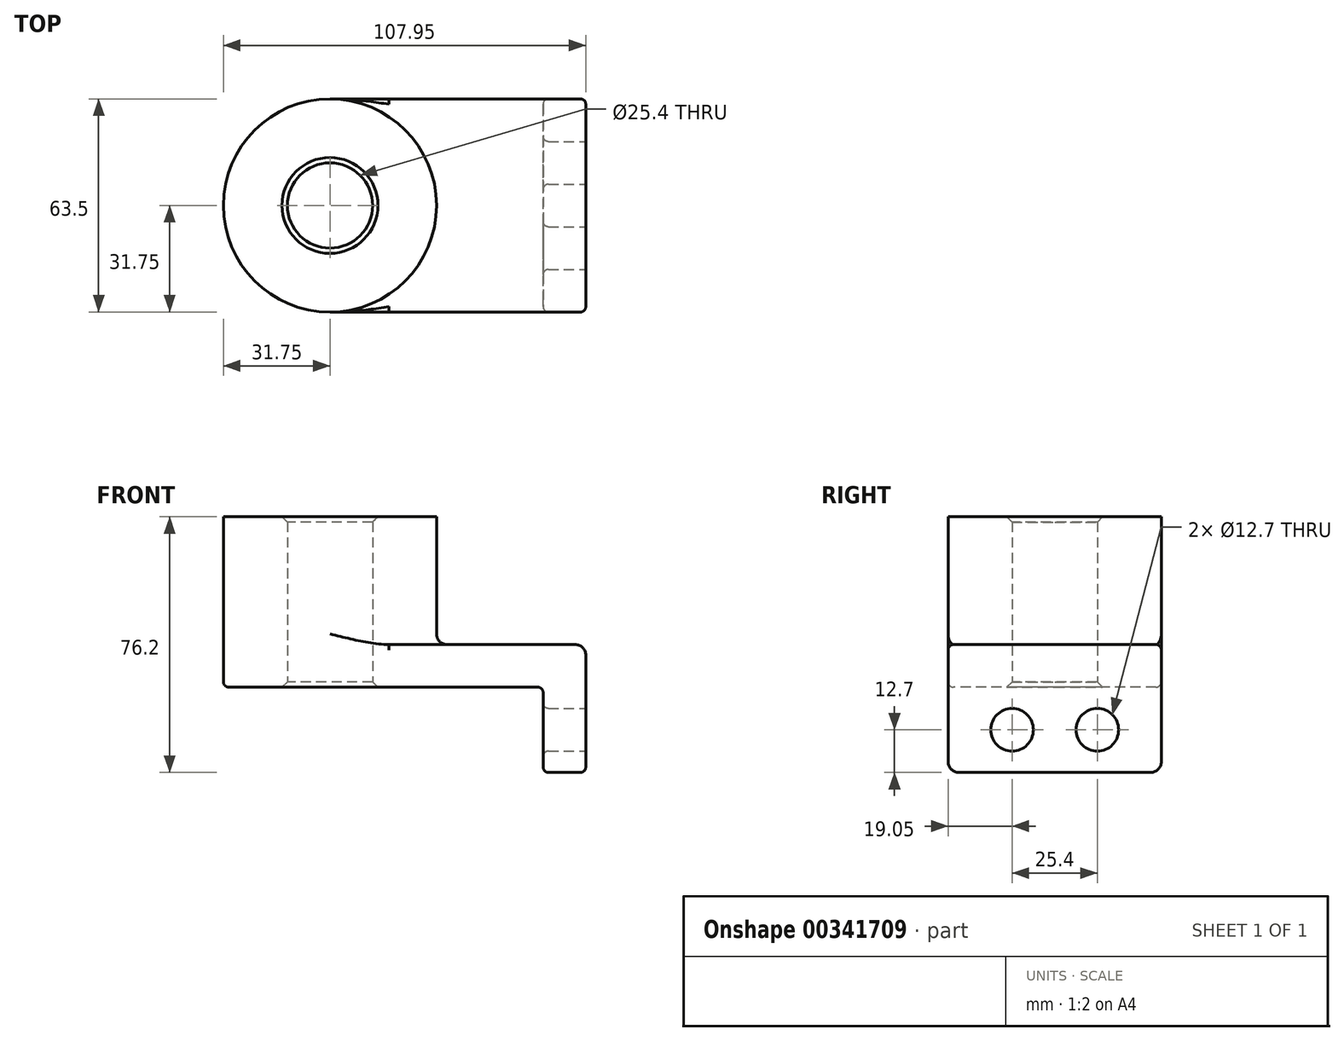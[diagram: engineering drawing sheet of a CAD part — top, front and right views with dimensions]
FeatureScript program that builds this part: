
annotation { "Feature Type Name" : "Feature", "Feature Type Description" : "" }
export const myFeature = defineFeature(function(context is Context, id is Id, definition is map)
    precondition{}
    {
        {
            var Q0;
            Q0=qCreatedBy(makeId("Top.planeOp"),FACE);
            var sketch = newSketch(context, id + "F0", { "sketchPlane" : qUnion([Q0])});
            skLineSegment(sketch, "E0.bottom", {"start": v(-38.1, 31.75) * mm, "end": v(38.1, 31.75) * mm});
            skLineSegment(sketch, "E0.top", {"start": v(-38.1, -31.75) * mm, "end": v(38.1, -31.75) * mm});
            skLineSegment(sketch, "E0.left", {"start": v(-38.1, 31.75) * mm, "end": v(-38.1, -31.75) * mm});
            skLineSegment(sketch, "E0.right", {"start": v(38.1, 31.75) * mm, "end": v(38.1, -31.75) * mm});
            skPoint(sketch, "E0.middle", {"position": v(0, 0) * mm});
            skCircle(sketch, "E1", {"center": v(-38.1, 0) * mm, "radius": 31.75 * mm});
            skPoint(sketch, "E1.centerSnap0", {"position": v(-38.1, 0) * mm});
            skCircle(sketch, "E2", {"center": v(-38.1, 0) * mm, "radius": 12.7 * mm});
            skSolve(sketch);
        }
        {
            var Q0;
            {var subQ1=sQuery(id+"F0.wireOp",EDGE,"E0.left");var subQ3=sQuery(id+"F0.wireOp",EDGE,"E2");var subQ4=makeQuery(id+"F0.imprint","INTERSECT",VERTEX,{"disambiguationData":[OD(0.0)],"derivedFrom":[subQ1,subQ3]});Q0=makeQuery(id+"F0.imprint","IMPRINT",FACE,{"disambiguationData":[TD([[makeQuery(id+"F0.imprint","IMPRINT",EDGE,{"disambiguationData":[TD([[subQ4,-1.0]])],"derivedFrom":subQ3}),-1.0]])]});}
            var Q1;
            {var subQ1=sQuery(id+"F0.wireOp",EDGE,"E0.left");var subQ3=sQuery(id+"F0.wireOp",EDGE,"E2");var subQ4=makeQuery(id+"F0.imprint","INTERSECT",VERTEX,{"disambiguationData":[OD(0.0)],"derivedFrom":[subQ1,subQ3]});Q1=makeQuery(id+"F0.imprint","IMPRINT",FACE,{"disambiguationData":[TD([[makeQuery(id+"F0.imprint","IMPRINT",EDGE,{"disambiguationData":[TD([[subQ4,1.0]])],"derivedFrom":subQ3}),-1.0]])]});}
            var Q2;
            {var subQ0=sQuery(id+"F0.wireOp",EDGE,"E0.bottom");Q2=makeQuery(id+"F0.imprint","IMPRINT",FACE,{"disambiguationData":[TD([[makeQuery(id+"F0.imprint","IMPRINT",EDGE,{"derivedFrom":subQ0}),-1.0]])]});}
            extrude(context, id + "F1", {"entities" : qUnion([Q0, Q1, Q2]), "depth" : 12.7 * mm});
        }
        {
            var Q0;
            {var subQ1=sQuery(id+"F0.wireOp",EDGE,"E0.left");var subQ3=sQuery(id+"F0.wireOp",EDGE,"E2");var subQ4=makeQuery(id+"F0.imprint","INTERSECT",VERTEX,{"disambiguationData":[OD(0.0)],"derivedFrom":[subQ1,subQ3]});Q0=makeQuery(id+"F0.imprint","IMPRINT",FACE,{"disambiguationData":[TD([[makeQuery(id+"F0.imprint","IMPRINT",EDGE,{"disambiguationData":[TD([[subQ4,1.0]])],"derivedFrom":subQ3}),-1.0]])]});}
            var Q1;
            {var subQ1=sQuery(id+"F0.wireOp",EDGE,"E0.left");var subQ3=sQuery(id+"F0.wireOp",EDGE,"E2");var subQ4=makeQuery(id+"F0.imprint","INTERSECT",VERTEX,{"disambiguationData":[OD(0.0)],"derivedFrom":[subQ1,subQ3]});Q1=makeQuery(id+"F0.imprint","IMPRINT",FACE,{"disambiguationData":[TD([[makeQuery(id+"F0.imprint","IMPRINT",EDGE,{"disambiguationData":[TD([[subQ4,-1.0]])],"derivedFrom":subQ3}),-1.0]])]});}
            extrude(context, id + "F2", {"entities" : qUnion([Q0, Q1]), "operationType" : NewBodyOperationType.ADD, "depth" : 50.8 * mm});
        }
        {
            var Q0;
            Q0=makeQuery(id+"F1.opExtrude","SWEPT_FACE",FACE,{"disambiguationData":[OSD([sQuery(id+"F0.wireOp",EDGE,"E0.right")])]});
            var sketch = newSketch(context, id + "F3", { "sketchPlane" : qUnion([Q0])});
            skLineSegment(sketch, "E3.top", {"start": v(-31.75, -25.4) * mm, "end": v(0.46, -25.4) * mm});
            skLineSegment(sketch, "E3.left", {"start": v(-31.75, 12.7) * mm, "end": v(-31.75, -25.4) * mm});
            skCircle(sketch, "E4", {"center": v(-12.7, -12.7) * mm, "radius": 6.35 * mm});
            skLineSegment(sketch, "E5", {"start": v(0, 0) * mm, "end": v(0, -25.4) * mm});
            skPoint(sketch, "E5.endSnap0", {"position": v(0.46, -25.4) * mm});
            skCircle(sketch, "E6.MirrorC", {"center": v(12.7, -12.7) * mm, "radius": 6.35 * mm});
            skPoint(sketch, "E7.orphan", {"position": v(32.68, -25.4) * mm});
            skPoint(sketch, "E8.end.orphan", {"position": v(0.46, -26.49) * mm});
            skLineSegment(sketch, "E9", {"start": v(0, -25.4) * mm, "end": v(31.75, -25.4) * mm});
            skLineSegment(sketch, "E10", {"start": v(31.75, -25.4) * mm, "end": v(31.75, 0) * mm});
            skLineSegment(sketch, "E11", {"start": v(31.75, 0) * mm, "end": v(-31.75, 0) * mm});
            skSolve(sketch);
        }
        {
            var Q0;
            {var subQ2=sQuery(id+"F3.wireOp",EDGE,"E5");Q0=makeQuery(id+"F3.imprint","IMPRINT",FACE,{"disambiguationData":[TD([[makeQuery(id+"F3.imprint","IMPRINT",EDGE,{"derivedFrom":subQ2}),1.0]])]});}
            var Q1;
            {var subQ4=sQuery(id+"F3.wireOp",EDGE,"E3.top");Q1=makeQuery(id+"F3.imprint","IMPRINT",FACE,{"disambiguationData":[TD([[makeQuery(id+"F3.imprint","IMPRINT",EDGE,{"derivedFrom":subQ4}),1.0]])]});}
            extrude(context, id + "F4", {"entities" : qUnion([Q0, Q1]), "operationType" : NewBodyOperationType.ADD, "depth" : -12.7 * mm});
        }
        {
            var Q0;
            Q0=makeQuery(id+"F1.opExtrude","CAP_EDGE",EDGE,{"disambiguationData":[OSD([sQuery(id+"F0.wireOp",EDGE,"E0.right")])],"isStart":false});
            var Q1;
            Q1=makeQuery(id+"F4.opExtrude","SWEPT_EDGE",EDGE,{"disambiguationData":[OSD([sQuery(id+"F3.wireOp",EDGE,"E3.top"),sQuery(id+"F3.wireOp",EDGE,"E3.left")])]});
            var Q2;
            {var subQ0=sQuery(id+"F0.wireOp",EDGE,"E1");Q2=makeQuery(id+"F2.boolean.opBoolean","INTERSECT",EDGE,{"derivedFrom":[makeQuery(id+"F1.opExtrude","CAP_FACE",FACE,{"disambiguationData":[OSD([sQuery(id+"F0.wireOp",EDGE,"E0.bottom"),sQuery(id+"F0.wireOp",EDGE,"E0.top"),sQuery(id+"F0.wireOp",EDGE,"E0.right"),subQ0,sQuery(id+"F0.wireOp",EDGE,"E2")])],"isStart":false}),makeQuery(id+"F2.opExtrude","SWEPT_FACE",FACE,{"disambiguationData":[OSD([subQ0])]})]});}
            var Q3;
            Q3=makeQuery(id+"F4.opExtrude","SWEPT_EDGE",EDGE,{"disambiguationData":[OSD([sQuery(id+"F3.wireOp",EDGE,"E9"),sQuery(id+"F3.wireOp",EDGE,"E10")])]});
            fillet(context, id + "F5", {"entities" : qUnion([Q0, Q1, Q2, Q3]), "radius" : 3.17 * mm, "tangentPropagation" : true, "allowEdgeOverflow" : false});
        }
        {
            var Q0;
            Q0=makeQuery(id+"F1.opExtrude","CAP_EDGE",EDGE,{"disambiguationData":[OSD([sQuery(id+"F0.wireOp",EDGE,"E0.top")])],"isStart":false});
            var Q1;
            Q1=makeQuery(id+"F1.opExtrude","CAP_EDGE",EDGE,{"disambiguationData":[OSD([sQuery(id+"F0.wireOp",EDGE,"E0.top")])],"isStart":true});
            var Q2;
            Q2=makeQuery(id+"F4.opExtrude","CAP_FACE",FACE,{"disambiguationData":[OSD([sQuery(id+"F3.wireOp",EDGE,"E3.top"),sQuery(id+"F3.wireOp",EDGE,"E3.left"),sQuery(id+"F3.wireOp",EDGE,"E4"),sQuery(id+"F3.wireOp",EDGE,"E6.MirrorC"),sQuery(id+"F3.wireOp",EDGE,"E9"),sQuery(id+"F3.wireOp",EDGE,"E10"),sQuery(id+"F3.wireOp",EDGE,"E11")])],"isStart":false});
            fillet(context, id + "F6", {"entities" : qUnion([Q0, Q1, Q2]), "radius" : 1.59 * mm, "tangentPropagation" : true, "allowEdgeOverflow" : false});
        }
        {
            var Q0;
            {var subQ0=sQuery(id+"F0.wireOp",EDGE,"E2");Q0=makeQuery(id+"F2.boolean.opBoolean","MERGE",FACE,{"derivedFrom":[makeQuery(id+"F1.opExtrude","SWEPT_FACE",FACE,{"disambiguationData":[OSD([subQ0])]}),makeQuery(id+"F2.opExtrude","SWEPT_FACE",FACE,{"disambiguationData":[OSD([subQ0])]})]});}
            chamfer(context, id + "F7", {"entities" : qUnion([Q0]), "width" : 1.59 * mm, "tangentPropagation" : true});
        }
    });
